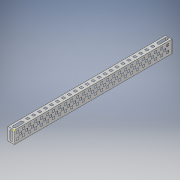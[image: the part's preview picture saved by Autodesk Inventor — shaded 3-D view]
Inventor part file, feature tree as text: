
AUTODESK INVENTOR PART (.ipt)
format: ipt  version: 2018 (Build 220112000, 112)  size: 580,608 bytes
history: native  units: in
note: dims shown in document units (in); Inventor stores cm internally (conversion verified against a paired STEP export)
features: sketch x13, extrude x8
ambient origin geometry x8: Origin, YZ Plane, XZ Plane, XY Plane, X Axis, Y Axis, Z Axis, Center Point
bodies: Solid1 (feature_tree), Solid2 (feature_tree), Solid3 (feature_tree), Solid4 (feature_tree)
feature tree (21):
  sketch  "Sketch1"  dims[d0=0.9843in d1=12.4016in]
  sketch  "Sketch2"  dims[d2=0.5118in d3=0.9843in]
  sketch  "Sketch3"  dims[d4=0.5118in d5=12.4016in]
  sketch  "Sketch4"  dims[d6=0.0039in d7=0.0in d8=0.0039in d9=0.0in]
  sketch  "Sketch5"  dims[d10=0.0039in d11=0.0in d12=0.5118in]
  sketch  "Sketch6"  dims[d13=0.9843in d14=0.0039in d15=0.0in]
  sketch  "Sketch7"  dims[d16=20.0in d17=0.0in d18=20.0in d19=0.0in]
  sketch  "Sketch8"  dims[d20=0.62in d21=90.0deg]
  extrude  "Extrusion1"  Depth=12.4016in
  extrude  "Extrusion2"  Depth=0.9843in
  extrude  "Extrusion3"  Depth=12.4016in
  extrude  "Extrusion4"  Depth=0.0039in TaperAngle=0.0deg
  extrude  "Extrusion5"  Depth=0.5118in
  extrude  "Extrusion6"  Depth=0.0039in TaperAngle=0.0deg
  extrude  "Extrusion7"  Depth=20.0in TaperAngle=0.0deg
  extrude  "Extrusion8"  TaperAngle=90.0deg  [1 undecoded]
  sketch  "Sketch9"  dims[d22=0.62in]
  sketch  "Sketch10"  dims[d23=0.18in]
  sketch  "Sketch11"  dims[d24=0.18in]
  sketch  "Sketch12"  dims[d25=0.3937in d27=1.0in d28=8.6614in d30=0.4685in]
  sketch  "Sketch13"  dims[d32=20.0in d33=0.0in d34=0.18in d35=0.18in d36=0.7874in d38=0.4724in d39=10.2362in d41=0.4724in d44=0.18in d45=0.18in d46=0.3937in d48=1.0in d49=9.8425in d51=0.4724in d53=20.0in d54=0.0in]
note: 1 required parameter value undecoded (feature->parameter linkage not recoverable at this tier; creation-order binding heuristic only, values carry confidence <= 0.55)
